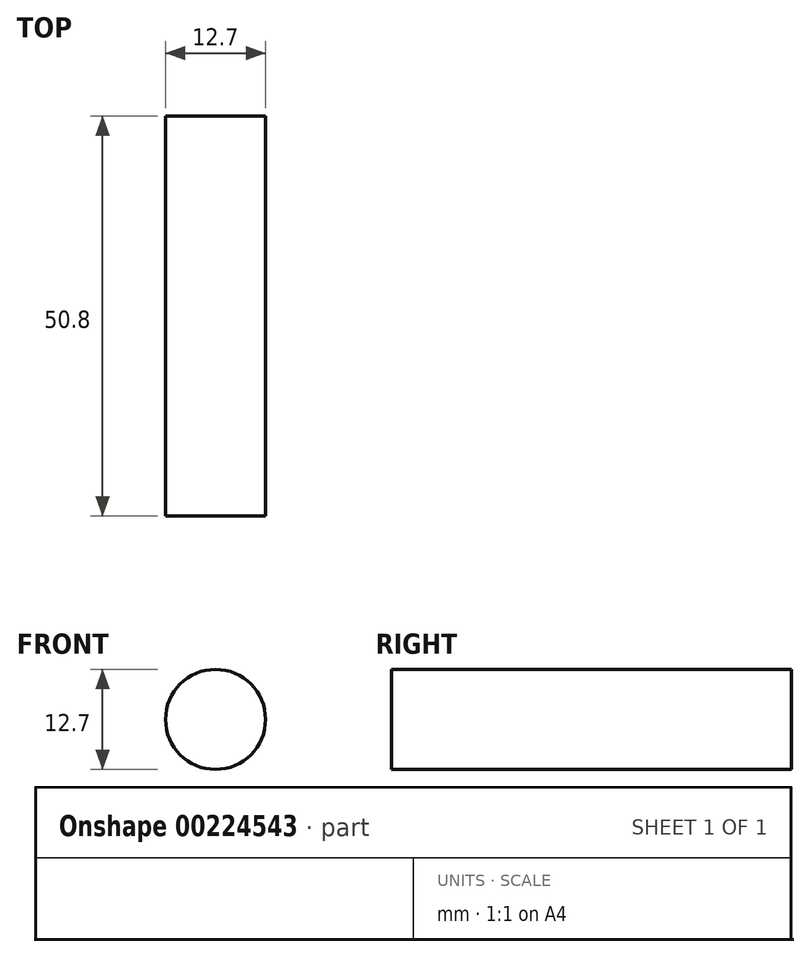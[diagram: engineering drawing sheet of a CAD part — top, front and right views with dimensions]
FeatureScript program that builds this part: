
annotation { "Feature Type Name" : "Feature", "Feature Type Description" : "" }
export const myFeature = defineFeature(function(context is Context, id is Id, definition is map)
    precondition{}
    {
        {
            var Q0;
            Q0=qCreatedBy(makeId("Front.planeOp"),FACE);
            var sketch = newSketch(context, id + "F0", { "sketchPlane" : qUnion([Q0])});
            skCircle(sketch, "E0", {"center": v(-43.73, 34.32) * mm, "radius": 6.35 * mm});
            skSolve(sketch);
        }
        {
            var Q0;
            Q0=makeQuery(id+"F0.imprint","IMPRINT",FACE,{"disambiguationData":[TD([[makeQuery(id+"F0.imprint","IMPRINT",EDGE,{"derivedFrom":sQuery(id+"F0.wireOp",EDGE,"E0")}),1.0]])]});
            extrude(context, id + "F1", {"entities" : qUnion([Q0]), "depth" : 50.8 * mm});
        }
    });
